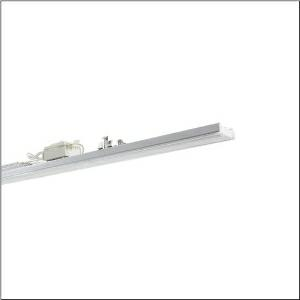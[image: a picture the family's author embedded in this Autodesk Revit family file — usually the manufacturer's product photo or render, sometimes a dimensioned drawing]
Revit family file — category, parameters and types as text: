
# Revit family: licross_r__21_recessed_mo_52tl11dn4axg_0374
name_source: partatom
category: Lighting Fixtures
units: mm (PartAtom-declared; Revit-internal decimal feet)

## family parameters
Cut with Voids When Loaded = No
Host = Face
Light Source = No
Part Type = Normal
Room Calculation Point = No
Round Connector Dimension = Use Diameter
Shared = No

## types (1)
- --- (1 x LED, 10120 lm, 58 W, 4000K)
    Apparent Load = 58 VA
    CIE Flux Codes = 89 96 99 100 100
    Color Rendering = 80
    Color Temperature = 4000K
    Default Elevation = 1800 mm
    Description = Licross® 21 Recessed MO, luminaire insert, of sheet steel, galvanised, coil coated, white, length: 1.500mm, width: 66mm, height: 67mm, LED rated luminous flux: 10.120lm, light colour: 840, control gear: DALI 2, with plug, 5-pole, with phase selection, mains connection: 220..240V, AC, 50/60Hz, rated input power: 58W, internal wiring halogen-free, primary light control with lens, of plastic, primary optical cover: cover, of PMMA, light emission: direct distribution, primary light characteristic: symmetric, protection rating (complete): IP40, insulation class (complete): insulation class I (protective earthing), certification: CE, ENEC, VDE, UKCA, protection symbol: D if used in an environment without relevant dust loads with corresponding accessories, impact resistance: IK06, permissible ambient temperature for indoor applications: -25..+40°C, corresponds to IFS (International Featured Standards) requirements for safety and quality in the food industry, reducing of maximum allowable ambient temperature of 5°C with ceiling mounting, LABS conformity tested according to VDMA 24364:2018-05, packaging unit: 1 piece
    Height = 58 mm
    Lamp = 1 x LED
    Lamp Light Flux = 10120 lm
    Lamp Power = 58 W
    Lamp count = 1
    Length = 1500 mm
    Luminous efficacy = 174 lm/W
    Manufacturer = Siteco
    ModVariant = No
    Model = 52TL11DN4AXG
    Mounting Place = Ceiling
    Mounting Type = Pendant
    Number of Poles = 1
    OnlyDefault = Yes
    Power Factor = 1
    Product Name = Licross® 21 Recessed MO
    Product group = luminaire insert | ceiling pendant
    ProductGroupID = 902
    Protection Class = Protection class I
    Protection Degree = IP 40
    RLX_Detail_Level = 1
    RLX_Emergency_Light_Flux = 0 lm
    RLX_Emergency_Type = 0
    RLX_Emergency_Type_DB = No
    RlxData = <blob elided: 24537 chars, md5=4dddb2c1>
    Socket = socket
    Standby Power = 0 W
    System Light Flux = 10120 lm
    System Power = 58 W
    Type Comments = factory setting: luminous flux: 100 % | dim-lin: 254 | 390 mA
    Type Image = l_1296930.jpg
    URL = http://relux.com
    VarID = @adj_148487
    Voltage = 0 V
    Weight = 0.00 kg
    Width = 66 mm

## geometry (parser evidence)
native form markers: Blend x4, Sweep x10
no freeform markers — native parametric forms only
